# Revit family: E 1500 LUM
name_source: partatom
category: Lighting Fixtures
revit_build: Autodesk Revit 2017 (Build: 20160225_1515(x64)
units: mm (PartAtom-declared; Revit-internal decimal feet)

## family parameters
Cut with Voids When Loaded = No
Host = Face
Light Source = Yes
Part Type = Normal
Room Calculation Point = No
Round Connector Dimension = Use Diameter
Shared = No

## types (3) — shared parameters
Color Filter = 16777215
Default Elevation = 1219 mm
Dimming Lamp Color Temperature Shift = <None>
Emit Shape Visible in Rendering = Yes
Emit from Rectangle Length = 1406 mm  [stored 4.61286 ft]
Emit from Rectangle Width = 54 mm  [stored 0.177165 ft]
Lamp = LED
Manufacturer = ARLIGHT AYDINLATMA A.Ş.
Model = E1500LUM
Tilt Angle = 90.00°
Type Comments = Industrial Lighting
URL = arlight.net/en/products/indoor/industrial-lighting-fixtures/lumo

## per-type parameters (varying)
| type | Apparent Load | Description | Photometric Web File | Wattage Comments |
| ELUM.1500.31.40 | 31 VA |  | e-1500-lum-31w-4k-80ra-rg-025.ies | 31W |
| ELUM.1500.43.40 | 43 VA |  | e-1500-lum-43w-4k-80ra-rg-035.ies | 43W |
| ELUM.1500.51.40 | 51 VA | High Lumen | e-1500-lum-51w-4k-80ra-rk-044.ies | 51W |

note: [stored X ft] marks values corroborated as IEEE doubles in the binary element streams (Revit-internal decimal feet)

## geometry (parser evidence)
native form markers: Blend x4, Sweep x2
no freeform markers — native parametric forms only
